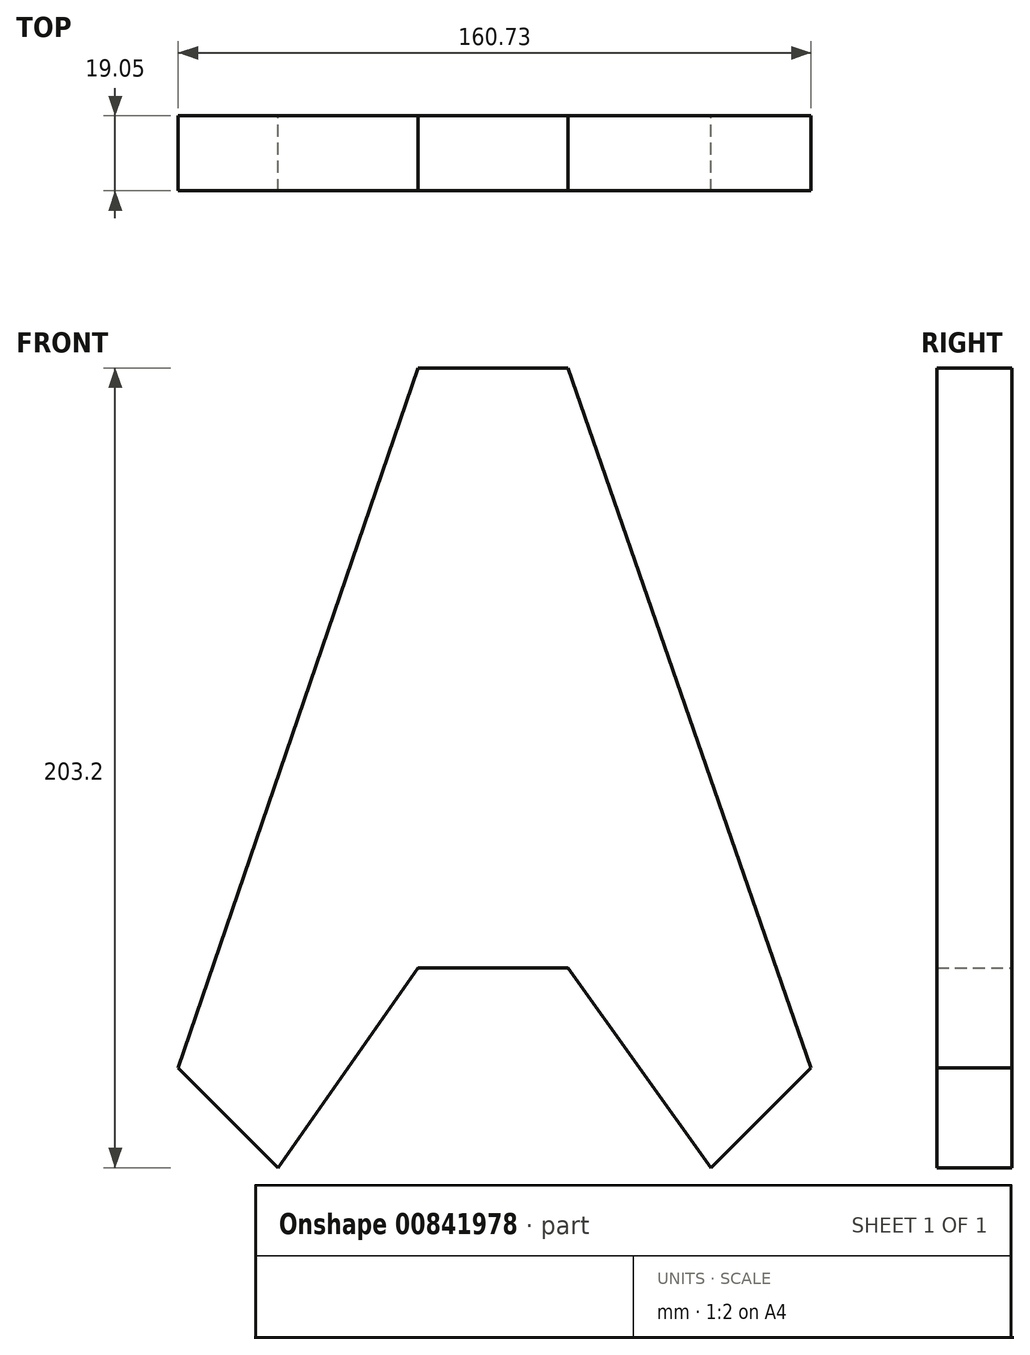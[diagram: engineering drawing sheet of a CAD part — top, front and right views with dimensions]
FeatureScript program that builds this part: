
annotation { "Feature Type Name" : "Feature", "Feature Type Description" : "" }
export const myFeature = defineFeature(function(context is Context, id is Id, definition is map)
    precondition{}
    {
        {
            var Q0;
            Q0=qCreatedBy(makeId("Front.planeOp"),FACE);
            var sketch = newSketch(context, id + "F0", { "sketchPlane" : qUnion([Q0])});
            skLineSegment(sketch, "E0", {"start": v(-19.58, 177.62) * mm, "end": v(18.52, 177.62) * mm});
            skLineSegment(sketch, "E1", {"start": v(18.52, 177.62) * mm, "end": v(80.19, -0.18) * mm});
            skLineSegment(sketch, "E2", {"start": v(80.19, -0.18) * mm, "end": v(54.79, -25.58) * mm});
            skLineSegment(sketch, "E3", {"start": v(54.79, -25.58) * mm, "end": v(18.52, 25.22) * mm});
            skLineSegment(sketch, "E4", {"start": v(18.52, 25.22) * mm, "end": v(-19.58, 25.22) * mm});
            skLineSegment(sketch, "E5", {"start": v(-19.58, 25.22) * mm, "end": v(-55.14, -25.58) * mm});
            skLineSegment(sketch, "E6", {"start": v(-55.14, -25.58) * mm, "end": v(-80.54, -0.18) * mm});
            skLineSegment(sketch, "E7", {"start": v(-80.54, -0.18) * mm, "end": v(-19.58, 177.62) * mm});
            skSolve(sketch);
        }
        {
            var Q0;
            Q0 = qSketchRegion(id + "F0", true);
            extrude(context, id + "F1", {"entities" : qUnion([Q0]), "depth" : 19.05 * mm, "offsetDistance" : 25.4 * mm});
        }
    });
